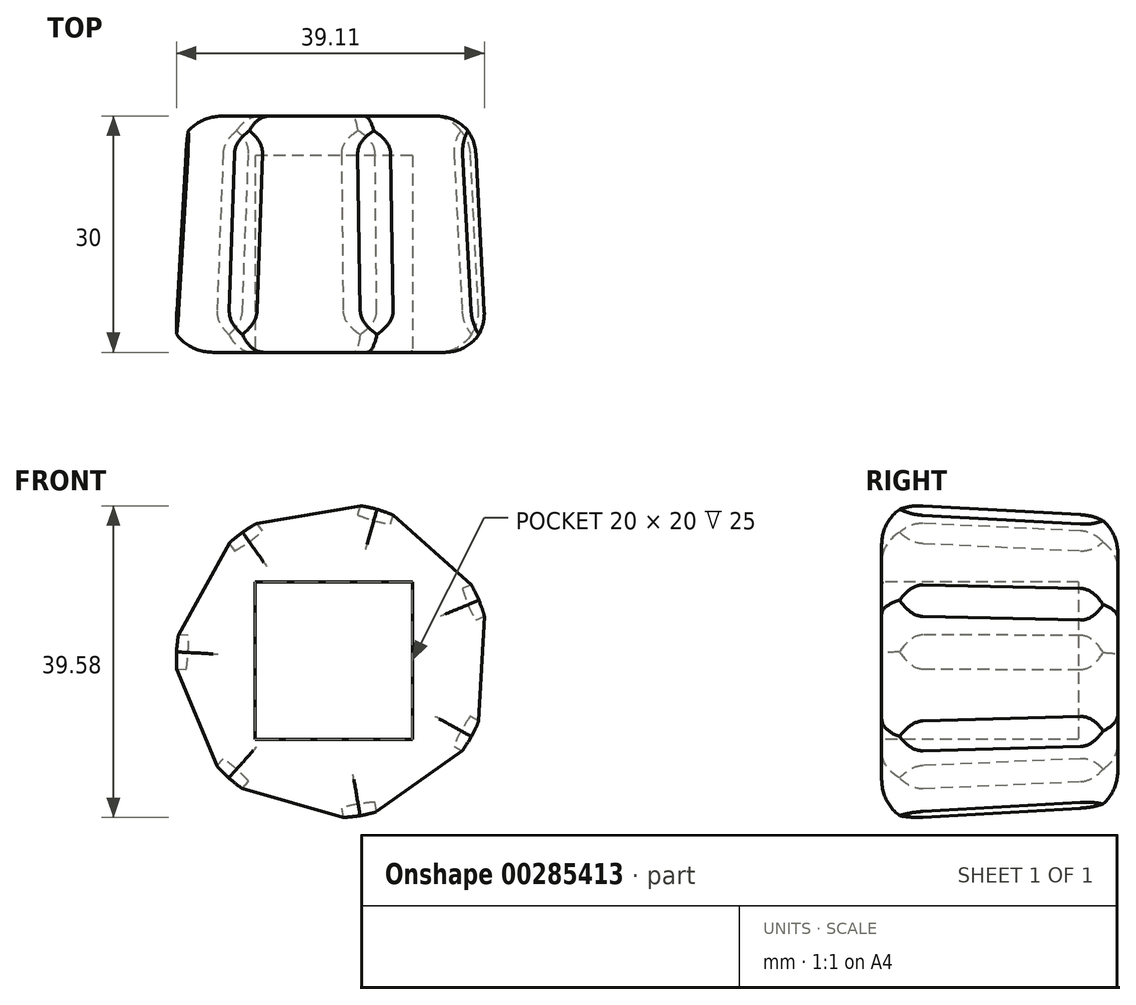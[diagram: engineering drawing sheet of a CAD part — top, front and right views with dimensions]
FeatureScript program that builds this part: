
annotation { "Feature Type Name" : "Feature", "Feature Type Description" : "" }
export const myFeature = defineFeature(function(context is Context, id is Id, definition is map)
    precondition{}
    {
        {
            var Q0;
            Q0=qCreatedBy(makeId("Front.planeOp"),FACE);
            var sketch = newSketch(context, id + "F0", { "sketchPlane" : qUnion([Q0])});
            skCircle(sketch, "E0.cCircle", {"center": v(0, 0) * mm, "radius": 17.5 * mm, "construction": true});
            skLineSegment(sketch, "E0.0", {"start": v(5.36, 18.67) * mm, "end": v(17.94, 7.45) * mm});
            skLineSegment(sketch, "E0.1", {"start": v(17.94, 7.45) * mm, "end": v(17, -9.38) * mm});
            skLineSegment(sketch, "E0.2", {"start": v(17, -9.38) * mm, "end": v(3.27, -19.15) * mm});
            skLineSegment(sketch, "E0.3", {"start": v(3.27, -19.15) * mm, "end": v(-12.93, -14.5) * mm});
            skLineSegment(sketch, "E0.4", {"start": v(-12.93, -14.5) * mm, "end": v(-19.4, 1.07) * mm});
            skLineSegment(sketch, "E0.5", {"start": v(-19.4, 1.07) * mm, "end": v(-11.25, 15.83) * mm});
            skLineSegment(sketch, "E0.6", {"start": v(-11.25, 15.83) * mm, "end": v(5.36, 18.67) * mm});
            skPoint(sketch, "E0.0.midPoint", {"position": v(11.65, 13.06) * mm});
            skSolve(sketch);
        }
        {
            var Q0;
            Q0 = qSketchRegion(id + "F0", true);
            extrude(context, id + "F1", {"entities" : qUnion([Q0]), "depth" : 30 * mm, "hasDraft" : true, "draftAngle" : 3 * degree});
        }
        {
            var Q0;
            Q0=makeQuery(id+"F1.opExtrude","CAP_FACE",FACE,{"disambiguationData":[OSD([sQuery(id+"F0.wireOp",EDGE,"E0.0"),sQuery(id+"F0.wireOp",EDGE,"E0.1"),sQuery(id+"F0.wireOp",EDGE,"E0.2"),sQuery(id+"F0.wireOp",EDGE,"E0.3"),sQuery(id+"F0.wireOp",EDGE,"E0.4"),sQuery(id+"F0.wireOp",EDGE,"E0.5"),sQuery(id+"F0.wireOp",EDGE,"E0.6")])],"isStart":false});
            fillet(context, id + "F2", {"entities" : qUnion([Q0]), "radius" : 5 * mm, "tangentPropagation" : true, "allowEdgeOverflow" : false});
        }
        {
            var Q0;
            Q0=makeQuery(id+"F1.opExtrude","CAP_FACE",FACE,{"disambiguationData":[OSD([sQuery(id+"F0.wireOp",EDGE,"E0.0"),sQuery(id+"F0.wireOp",EDGE,"E0.1"),sQuery(id+"F0.wireOp",EDGE,"E0.2"),sQuery(id+"F0.wireOp",EDGE,"E0.3"),sQuery(id+"F0.wireOp",EDGE,"E0.4"),sQuery(id+"F0.wireOp",EDGE,"E0.5"),sQuery(id+"F0.wireOp",EDGE,"E0.6")])],"isStart":true});
            fillet(context, id + "F3", {"entities" : qUnion([Q0]), "radius" : 5 * mm, "tangentPropagation" : true, "allowEdgeOverflow" : false});
        }
        {
            var Q0;
            Q0=makeQuery(id+"F1.opExtrude","CAP_FACE",FACE,{"disambiguationData":[OSD([sQuery(id+"F0.wireOp",EDGE,"E0.0"),sQuery(id+"F0.wireOp",EDGE,"E0.1"),sQuery(id+"F0.wireOp",EDGE,"E0.2"),sQuery(id+"F0.wireOp",EDGE,"E0.3"),sQuery(id+"F0.wireOp",EDGE,"E0.4"),sQuery(id+"F0.wireOp",EDGE,"E0.5"),sQuery(id+"F0.wireOp",EDGE,"E0.6")])],"isStart":false});
            var sketch = newSketch(context, id + "F4", { "sketchPlane" : qUnion([Q0])});
            skLineSegment(sketch, "E1.bottom", {"start": v(10, 10) * mm, "end": v(-10, 10) * mm});
            skLineSegment(sketch, "E1.top", {"start": v(10, -10) * mm, "end": v(-10, -10) * mm});
            skLineSegment(sketch, "E1.left", {"start": v(10, 10) * mm, "end": v(10, -10) * mm});
            skLineSegment(sketch, "E1.right", {"start": v(-10, 10) * mm, "end": v(-10, -10) * mm});
            skPoint(sketch, "E1.middle", {"position": v(0, 0) * mm});
            skSolve(sketch);
        }
        {
            var Q0;
            Q0 = qSketchRegion(id + "F4", true);
            extrude(context, id + "F5", {"entities" : qUnion([Q0]), "operationType" : NewBodyOperationType.REMOVE, "oppositeDirection" : true, "depth" : 25 * mm});
        }
        {
            var Q0;
            Q0=makeQuery(id+"F1.opExtrude","SWEPT_FACE",FACE,{"disambiguationData":[OSD([sQuery(id+"F0.wireOp",EDGE,"E0.5")])]});
            var Q1;
            Q1=makeQuery(id+"F1.opExtrude","SWEPT_FACE",FACE,{"disambiguationData":[OSD([sQuery(id+"F0.wireOp",EDGE,"E0.6")])]});
            var Q2;
            Q2=makeQuery(id+"F1.opExtrude","SWEPT_FACE",FACE,{"disambiguationData":[OSD([sQuery(id+"F0.wireOp",EDGE,"E0.4")])]});
            var Q3;
            Q3=makeQuery(id+"F1.opExtrude","SWEPT_FACE",FACE,{"disambiguationData":[OSD([sQuery(id+"F0.wireOp",EDGE,"E0.3")])]});
            var Q4;
            Q4=makeQuery(id+"F1.opExtrude","SWEPT_FACE",FACE,{"disambiguationData":[OSD([sQuery(id+"F0.wireOp",EDGE,"E0.2")])]});
            var Q5;
            Q5=makeQuery(id+"F1.opExtrude","SWEPT_FACE",FACE,{"disambiguationData":[OSD([sQuery(id+"F0.wireOp",EDGE,"E0.1")])]});
            var Q6;
            Q6=makeQuery(id+"F1.opExtrude","SWEPT_FACE",FACE,{"disambiguationData":[OSD([sQuery(id+"F0.wireOp",EDGE,"E0.0")])]});
            chamfer(context, id + "F6", {"entities" : qUnion([Q0, Q1, Q2, Q3, Q4, Q5, Q6]), "width" : 5 * mm, "tangentPropagation" : true});
        }
    });
